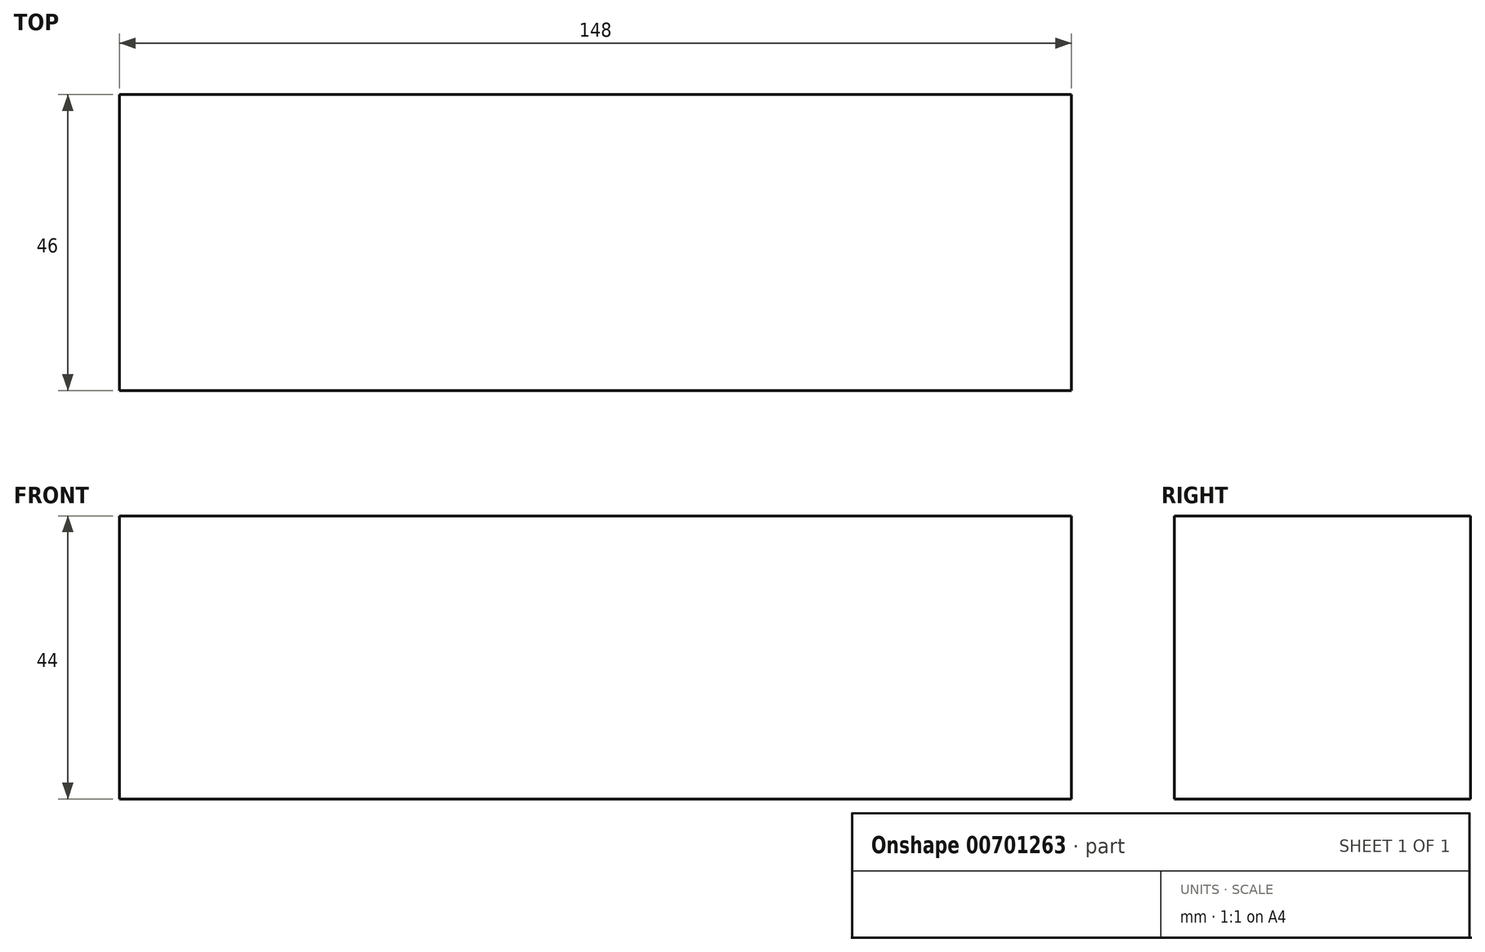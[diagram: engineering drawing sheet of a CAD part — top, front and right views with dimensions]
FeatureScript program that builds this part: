
annotation { "Feature Type Name" : "Feature", "Feature Type Description" : "" }
export const myFeature = defineFeature(function(context is Context, id is Id, definition is map)
    precondition{}
    {
        {
            var Q0;
            Q0=qCreatedBy(makeId("Front.planeOp"),FACE);
            var sketch = newSketch(context, id + "F0", { "sketchPlane" : qUnion([Q0])});
            skLineSegment(sketch, "E0.bottom", {"start": v(0, 0) * mm, "end": v(148, 0) * mm});
            skLineSegment(sketch, "E0.top", {"start": v(0, 44) * mm, "end": v(148, 44) * mm});
            skLineSegment(sketch, "E0.left", {"start": v(0, 0) * mm, "end": v(0, 44) * mm});
            skLineSegment(sketch, "E0.right", {"start": v(148, 0) * mm, "end": v(148, 44) * mm});
            skSolve(sketch);
        }
        {
            var Q0;
            Q0=makeQuery(id+"F0.imprint","IMPRINT",FACE,{"disambiguationData":[TD([[makeQuery(id+"F0.imprint","IMPRINT",EDGE,{"derivedFrom":sQuery(id+"F0.wireOp",EDGE,"E0.bottom")}),1.0]])]});
            extrude(context, id + "F1", {"entities" : qUnion([Q0]), "depth" : 46 * mm, "offsetDistance" : 25 * mm});
        }
    });
